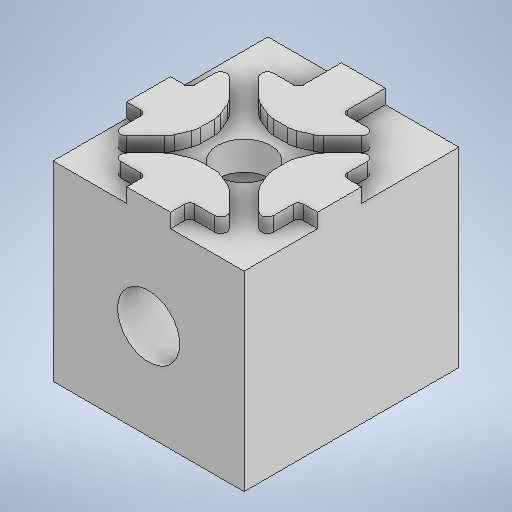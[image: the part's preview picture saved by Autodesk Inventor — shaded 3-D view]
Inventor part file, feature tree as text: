
AUTODESK INVENTOR PART (.ipt)
format: ipt  version: 2025 (Build 290162010, 162A)  size: 442,880 bytes
history: native  units: in
note: dims shown in document units (in); Inventor stores cm internally (conversion verified against a paired STEP export)
features: extrude x5, sketch x5, fillet x1, other x1
ambient origin geometry x8: Origin, YZ Plane, XZ Plane, XY Plane, X Axis, Y Axis, Z Axis, Center Point
bodies: Body1 (feature_tree)
feature tree (12):
  extrude  "Extrusion10"  Depth=0.7874in
  extrude  "Extrusion11"  Depth=0.7874in TaperAngle=0.0deg
  fillet  "Rundung3"  Radius=0.1811in
  other  "Verdickung1"
  extrude  "Extrusion12"  Depth=0.0498in
  extrude  "Extrusion13"  Depth=0.0834in
  extrude  "Extrusion14"  Depth=0.3937in
  sketch  "Skizze10"  dims[d78=0.7874in d79=0.7874in]
  sketch  "Skizze11"  dims[d80=0.2205in d81=0.7874in d82=0.0in d83=0.1811in]
  sketch  "Skizze13"  dims[d85=0.0394in d87=0.0498in]
  sketch  "Skizze14"  dims[d89=45.0deg d90=0.0834in]
  sketch  "Skizze15"  dims[d91=45.0deg d92=0.1253in d93=0.0893in d94=0.2421in d95=0.0591in d96=0.0in d97=0.0787in d98=0.1811in d102=45.0deg d104=45.0deg d107=0.2421in d108=0.1811in d112=45.0deg d114=45.0deg d117=0.2421in d118=0.1811in d119=0.0394in d122=45.0deg d124=45.0deg d127=0.2421in d128=0.0591in d129=0.0984in d130=0.0984in d131=0.3937in d132=0.6693in d133=0.0in d134=0.6398in d135=0.2067in d136=0.0in d137=0.2559in d138=0.0in d139=0.0in]
